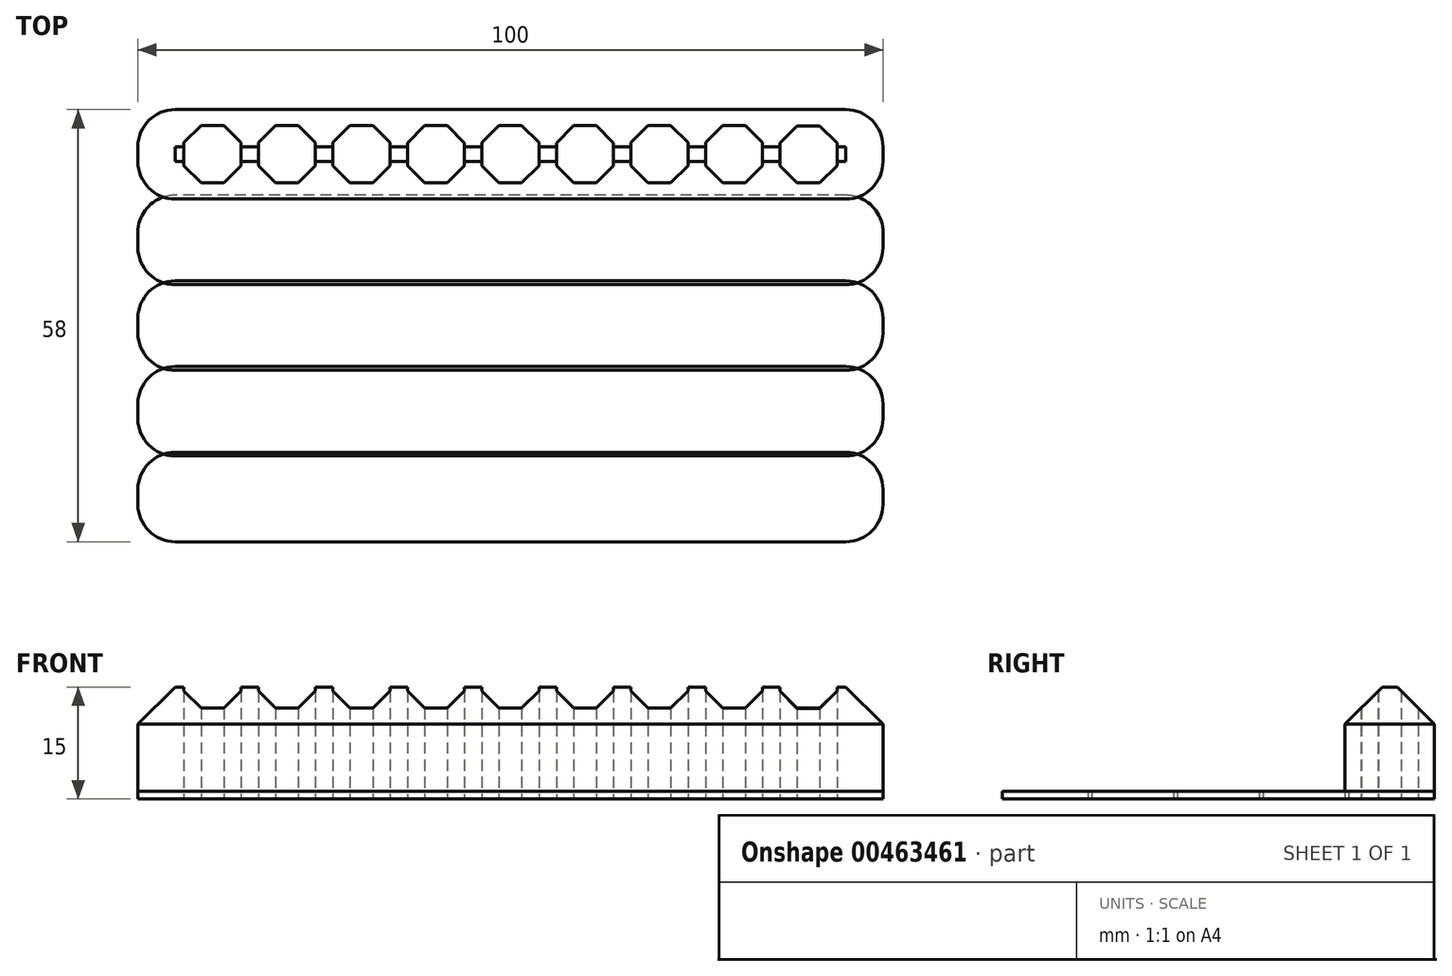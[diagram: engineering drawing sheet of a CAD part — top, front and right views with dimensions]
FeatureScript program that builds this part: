
annotation { "Feature Type Name" : "Feature", "Feature Type Description" : "" }
export const myFeature = defineFeature(function(context is Context, id is Id, definition is map)
    precondition{}
    {
        {
            var Q0;
            Q0=qCreatedBy(makeId("Top.planeOp"),FACE);
            var sketch = newSketch(context, id + "F0", { "sketchPlane" : qUnion([Q0])});
            skLineSegment(sketch, "E0.bottom", {"start": v(50, -6) * mm, "end": v(-50, -6) * mm});
            skLineSegment(sketch, "E0.top", {"start": v(50, 6) * mm, "end": v(-50, 6) * mm});
            skLineSegment(sketch, "E0.left", {"start": v(50, -6) * mm, "end": v(50, 6) * mm});
            skLineSegment(sketch, "E0.right", {"start": v(-50, -6) * mm, "end": v(-50, 6) * mm});
            skPoint(sketch, "E0.middle", {"position": v(0, 0) * mm});
            skPoint(sketch, "E1.middle", {"position": v(-40, 0) * mm});
            skLineSegment(sketch, "E2.bottom", {"start": v(-41.53, 3.83) * mm, "end": v(-38.47, 3.83) * mm});
            skLineSegment(sketch, "E2.top", {"start": v(-41.53, -3.83) * mm, "end": v(-38.47, -3.83) * mm});
            skLineSegment(sketch, "E2.left", {"start": v(-41.53, 3.83) * mm, "end": v(-41.53, -3.83) * mm});
            skLineSegment(sketch, "E2.right", {"start": v(-38.47, 3.83) * mm, "end": v(-38.47, -3.83) * mm});
            skLineSegment(sketch, "E3.bottom", {"start": v(-36.17, -1.54) * mm, "end": v(-43.83, -1.54) * mm});
            skLineSegment(sketch, "E3.top", {"start": v(-36.17, 1.54) * mm, "end": v(-43.83, 1.54) * mm});
            skLineSegment(sketch, "E3.left", {"start": v(-36.17, -1.54) * mm, "end": v(-36.17, 1.54) * mm});
            skLineSegment(sketch, "E3.right", {"start": v(-43.83, -1.54) * mm, "end": v(-43.83, 1.54) * mm});
            skPoint(sketch, "E4.middle", {"position": v(-30, 0) * mm});
            skLineSegment(sketch, "E5.bottom", {"start": v(-31.53, 3.83) * mm, "end": v(-28.47, 3.83) * mm});
            skLineSegment(sketch, "E5.top", {"start": v(-31.53, -3.83) * mm, "end": v(-28.47, -3.83) * mm});
            skLineSegment(sketch, "E5.left", {"start": v(-31.53, 3.83) * mm, "end": v(-31.53, -3.83) * mm});
            skLineSegment(sketch, "E5.right", {"start": v(-28.47, 3.83) * mm, "end": v(-28.47, -3.83) * mm});
            skLineSegment(sketch, "E6.bottom", {"start": v(-26.17, -1.54) * mm, "end": v(-33.83, -1.54) * mm});
            skLineSegment(sketch, "E6.top", {"start": v(-26.17, 1.54) * mm, "end": v(-33.83, 1.54) * mm});
            skLineSegment(sketch, "E6.left", {"start": v(-26.17, -1.54) * mm, "end": v(-26.17, 1.54) * mm});
            skLineSegment(sketch, "E6.right", {"start": v(-33.83, -1.54) * mm, "end": v(-33.83, 1.54) * mm});
            skPoint(sketch, "E7.middle", {"position": v(-20, 0) * mm});
            skLineSegment(sketch, "E8.bottom", {"start": v(-21.53, 3.84) * mm, "end": v(-18.48, 3.84) * mm});
            skLineSegment(sketch, "E8.top", {"start": v(-21.53, -3.83) * mm, "end": v(-18.48, -3.83) * mm});
            skLineSegment(sketch, "E8.left", {"start": v(-21.53, 3.84) * mm, "end": v(-21.53, -3.83) * mm});
            skLineSegment(sketch, "E8.right", {"start": v(-18.48, 3.84) * mm, "end": v(-18.48, -3.83) * mm});
            skLineSegment(sketch, "E9.bottom", {"start": v(-16.18, -1.53) * mm, "end": v(-23.83, -1.53) * mm});
            skLineSegment(sketch, "E9.top", {"start": v(-16.18, 1.54) * mm, "end": v(-23.83, 1.54) * mm});
            skLineSegment(sketch, "E9.left", {"start": v(-16.18, -1.53) * mm, "end": v(-16.18, 1.54) * mm});
            skLineSegment(sketch, "E9.right", {"start": v(-23.83, -1.53) * mm, "end": v(-23.83, 1.54) * mm});
            skPoint(sketch, "E10.middle", {"position": v(-9.99, 0) * mm});
            skLineSegment(sketch, "E11.bottom", {"start": v(-11.52, 3.83) * mm, "end": v(-8.46, 3.83) * mm});
            skLineSegment(sketch, "E11.top", {"start": v(-11.52, -3.84) * mm, "end": v(-8.46, -3.84) * mm});
            skLineSegment(sketch, "E11.left", {"start": v(-11.52, 3.83) * mm, "end": v(-11.52, -3.84) * mm});
            skLineSegment(sketch, "E11.right", {"start": v(-8.46, 3.83) * mm, "end": v(-8.46, -3.84) * mm});
            skLineSegment(sketch, "E12.bottom", {"start": v(-6.16, -1.54) * mm, "end": v(-13.82, -1.54) * mm});
            skLineSegment(sketch, "E12.top", {"start": v(-6.16, 1.53) * mm, "end": v(-13.82, 1.53) * mm});
            skLineSegment(sketch, "E12.left", {"start": v(-6.16, -1.54) * mm, "end": v(-6.16, 1.53) * mm});
            skLineSegment(sketch, "E12.right", {"start": v(-13.82, -1.54) * mm, "end": v(-13.82, 1.53) * mm});
            skPoint(sketch, "E13.middle", {"position": v(0, 0.02) * mm});
            skLineSegment(sketch, "E14.bottom", {"start": v(-1.53, 3.86) * mm, "end": v(1.52, 3.86) * mm});
            skLineSegment(sketch, "E14.top", {"start": v(-1.53, -3.8) * mm, "end": v(1.52, -3.8) * mm});
            skLineSegment(sketch, "E14.left", {"start": v(-1.53, 3.86) * mm, "end": v(-1.53, -3.8) * mm});
            skLineSegment(sketch, "E14.right", {"start": v(1.52, 3.86) * mm, "end": v(1.52, -3.8) * mm});
            skLineSegment(sketch, "E15.bottom", {"start": v(3.82, -1.51) * mm, "end": v(-3.83, -1.51) * mm});
            skLineSegment(sketch, "E15.top", {"start": v(3.82, 1.56) * mm, "end": v(-3.83, 1.56) * mm});
            skLineSegment(sketch, "E15.left", {"start": v(3.82, -1.51) * mm, "end": v(3.82, 1.56) * mm});
            skLineSegment(sketch, "E15.right", {"start": v(-3.83, -1.51) * mm, "end": v(-3.83, 1.56) * mm});
            skPoint(sketch, "E16.middle", {"position": v(10, 0) * mm});
            skLineSegment(sketch, "E17.bottom", {"start": v(8.48, 3.83) * mm, "end": v(11.53, 3.83) * mm});
            skLineSegment(sketch, "E17.top", {"start": v(8.48, -3.84) * mm, "end": v(11.53, -3.84) * mm});
            skLineSegment(sketch, "E17.left", {"start": v(8.48, 3.83) * mm, "end": v(8.48, -3.84) * mm});
            skLineSegment(sketch, "E17.right", {"start": v(11.53, 3.83) * mm, "end": v(11.53, -3.84) * mm});
            skLineSegment(sketch, "E18.bottom", {"start": v(13.83, -1.54) * mm, "end": v(6.18, -1.54) * mm});
            skLineSegment(sketch, "E18.top", {"start": v(13.83, 1.53) * mm, "end": v(6.18, 1.53) * mm});
            skLineSegment(sketch, "E18.left", {"start": v(13.83, -1.54) * mm, "end": v(13.83, 1.53) * mm});
            skLineSegment(sketch, "E18.right", {"start": v(6.18, -1.54) * mm, "end": v(6.18, 1.53) * mm});
            skPoint(sketch, "E19.middle", {"position": v(19.99, 0) * mm});
            skLineSegment(sketch, "E20.bottom", {"start": v(18.46, 3.84) * mm, "end": v(21.51, 3.84) * mm});
            skLineSegment(sketch, "E20.top", {"start": v(18.46, -3.82) * mm, "end": v(21.51, -3.82) * mm});
            skLineSegment(sketch, "E20.left", {"start": v(18.46, 3.84) * mm, "end": v(18.46, -3.82) * mm});
            skLineSegment(sketch, "E20.right", {"start": v(21.51, 3.84) * mm, "end": v(21.51, -3.82) * mm});
            skLineSegment(sketch, "E21.bottom", {"start": v(23.82, -1.53) * mm, "end": v(16.16, -1.53) * mm});
            skLineSegment(sketch, "E21.top", {"start": v(23.82, 1.55) * mm, "end": v(16.16, 1.55) * mm});
            skLineSegment(sketch, "E21.left", {"start": v(23.82, -1.53) * mm, "end": v(23.82, 1.55) * mm});
            skLineSegment(sketch, "E21.right", {"start": v(16.16, -1.53) * mm, "end": v(16.16, 1.55) * mm});
            skPoint(sketch, "E22.middle", {"position": v(30, 0) * mm});
            skLineSegment(sketch, "E23.bottom", {"start": v(28.47, 3.84) * mm, "end": v(31.53, 3.84) * mm});
            skLineSegment(sketch, "E23.top", {"start": v(28.47, -3.82) * mm, "end": v(31.53, -3.82) * mm});
            skLineSegment(sketch, "E23.left", {"start": v(28.47, 3.84) * mm, "end": v(28.47, -3.82) * mm});
            skLineSegment(sketch, "E23.right", {"start": v(31.53, 3.84) * mm, "end": v(31.53, -3.82) * mm});
            skLineSegment(sketch, "E24.bottom", {"start": v(33.83, -1.53) * mm, "end": v(26.17, -1.53) * mm});
            skLineSegment(sketch, "E24.top", {"start": v(33.83, 1.55) * mm, "end": v(26.17, 1.55) * mm});
            skLineSegment(sketch, "E24.left", {"start": v(33.83, -1.53) * mm, "end": v(33.83, 1.55) * mm});
            skLineSegment(sketch, "E24.right", {"start": v(26.17, -1.53) * mm, "end": v(26.17, 1.55) * mm});
            skPoint(sketch, "E25.middle", {"position": v(40, -0.02) * mm});
            skLineSegment(sketch, "E26.bottom", {"start": v(38.47, 3.81) * mm, "end": v(41.52, 3.81) * mm});
            skLineSegment(sketch, "E26.top", {"start": v(38.47, -3.85) * mm, "end": v(41.52, -3.85) * mm});
            skLineSegment(sketch, "E26.left", {"start": v(38.47, 3.81) * mm, "end": v(38.47, -3.85) * mm});
            skLineSegment(sketch, "E26.right", {"start": v(41.52, 3.81) * mm, "end": v(41.52, -3.85) * mm});
            skLineSegment(sketch, "E27.bottom", {"start": v(43.82, -1.56) * mm, "end": v(36.17, -1.56) * mm});
            skLineSegment(sketch, "E27.top", {"start": v(43.82, 1.52) * mm, "end": v(36.17, 1.52) * mm});
            skLineSegment(sketch, "E27.left", {"start": v(43.82, -1.56) * mm, "end": v(43.82, 1.52) * mm});
            skLineSegment(sketch, "E27.right", {"start": v(36.17, -1.56) * mm, "end": v(36.17, 1.52) * mm});
            skLineSegment(sketch, "E28", {"start": v(-41.53, 3.83) * mm, "end": v(-43.83, 1.54) * mm});
            skLineSegment(sketch, "E29", {"start": v(-43.83, -1.54) * mm, "end": v(-41.53, -3.83) * mm});
            skLineSegment(sketch, "E30", {"start": v(-38.47, -3.83) * mm, "end": v(-36.17, -1.54) * mm});
            skLineSegment(sketch, "E31", {"start": v(-36.17, 1.54) * mm, "end": v(-38.47, 3.83) * mm});
            skLineSegment(sketch, "E32", {"start": v(-33.83, 1.54) * mm, "end": v(-31.53, 3.83) * mm});
            skLineSegment(sketch, "E33", {"start": v(-28.47, 3.83) * mm, "end": v(-26.17, 1.54) * mm});
            skLineSegment(sketch, "E34", {"start": v(-26.17, -1.54) * mm, "end": v(-28.47, -3.83) * mm});
            skLineSegment(sketch, "E35", {"start": v(-31.53, -3.83) * mm, "end": v(-33.83, -1.54) * mm});
            skLineSegment(sketch, "E36", {"start": v(-23.83, 1.54) * mm, "end": v(-21.53, 3.84) * mm});
            skLineSegment(sketch, "E37", {"start": v(-18.48, 3.84) * mm, "end": v(-16.18, 1.54) * mm});
            skLineSegment(sketch, "E38", {"start": v(-16.18, -1.53) * mm, "end": v(-18.48, -3.83) * mm});
            skLineSegment(sketch, "E39", {"start": v(-21.53, -3.83) * mm, "end": v(-23.83, -1.53) * mm});
            skLineSegment(sketch, "E40", {"start": v(-13.82, -1.54) * mm, "end": v(-11.52, -3.84) * mm});
            skLineSegment(sketch, "E41", {"start": v(-13.82, 1.53) * mm, "end": v(-11.52, 3.83) * mm});
            skLineSegment(sketch, "E42", {"start": v(-8.46, 3.83) * mm, "end": v(-6.16, 1.53) * mm});
            skLineSegment(sketch, "E43", {"start": v(-6.16, -1.54) * mm, "end": v(-8.46, -3.84) * mm});
            skLineSegment(sketch, "E44", {"start": v(-3.83, -1.51) * mm, "end": v(-1.53, -3.8) * mm});
            skLineSegment(sketch, "E45", {"start": v(-3.83, 1.56) * mm, "end": v(-1.53, 3.86) * mm});
            skLineSegment(sketch, "E46", {"start": v(1.52, 3.86) * mm, "end": v(3.82, 1.56) * mm});
            skLineSegment(sketch, "E47", {"start": v(3.82, -1.51) * mm, "end": v(1.52, -3.8) * mm});
            skLineSegment(sketch, "E48", {"start": v(6.18, 1.53) * mm, "end": v(8.48, 3.83) * mm});
            skLineSegment(sketch, "E49", {"start": v(11.53, 3.83) * mm, "end": v(13.83, 1.53) * mm});
            skLineSegment(sketch, "E50", {"start": v(13.83, -1.54) * mm, "end": v(11.53, -3.84) * mm});
            skLineSegment(sketch, "E51", {"start": v(8.48, -3.84) * mm, "end": v(6.18, -1.54) * mm});
            skLineSegment(sketch, "E52", {"start": v(16.16, 1.55) * mm, "end": v(18.46, 3.84) * mm});
            skLineSegment(sketch, "E53", {"start": v(21.51, 3.84) * mm, "end": v(23.82, 1.55) * mm});
            skLineSegment(sketch, "E54", {"start": v(23.82, -1.53) * mm, "end": v(21.51, -3.82) * mm});
            skLineSegment(sketch, "E55", {"start": v(18.46, -3.82) * mm, "end": v(16.16, -1.53) * mm});
            skLineSegment(sketch, "E56", {"start": v(26.17, 1.55) * mm, "end": v(28.47, 3.84) * mm});
            skLineSegment(sketch, "E57", {"start": v(31.53, 3.84) * mm, "end": v(33.83, 1.55) * mm});
            skLineSegment(sketch, "E58", {"start": v(33.83, -1.53) * mm, "end": v(31.53, -3.82) * mm});
            skLineSegment(sketch, "E59", {"start": v(28.47, -3.82) * mm, "end": v(26.17, -1.53) * mm});
            skLineSegment(sketch, "E60", {"start": v(36.17, 1.52) * mm, "end": v(38.47, 3.81) * mm});
            skLineSegment(sketch, "E61", {"start": v(41.52, 3.81) * mm, "end": v(43.82, 1.52) * mm});
            skLineSegment(sketch, "E62", {"start": v(43.82, -1.56) * mm, "end": v(41.52, -3.85) * mm});
            skLineSegment(sketch, "E63", {"start": v(38.47, -3.85) * mm, "end": v(36.17, -1.56) * mm});
            skSolve(sketch);
        }
        {
            var Q0;
            Q0=makeQuery(id+"F0.imprint","IMPRINT",FACE,{"disambiguationData":[TD([[makeQuery(id+"F0.imprint","IMPRINT",EDGE,{"derivedFrom":sQuery(id+"F0.wireOp",EDGE,"E0.bottom")}),-1.0]])]});
            extrude(context, id + "F1", {"entities" : qUnion([Q0]), "depth" : 15 * mm});
        }
        {
            var Q0;
            Q0=makeQuery(id+"F0.imprint","IMPRINT",FACE,{"disambiguationData":[TD([[makeQuery(id+"F0.imprint","IMPRINT",EDGE,{"derivedFrom":sQuery(id+"F0.wireOp",EDGE,"E0.bottom")}),-1.0]])]});
            var Q1;
            {var subQ5=sQuery(id+"F0.wireOp",EDGE,"E3.right");Q1=makeQuery(id+"F0.imprint","IMPRINT",FACE,{"disambiguationData":[TD([[makeQuery(id+"F0.imprint","IMPRINT",EDGE,{"derivedFrom":subQ5}),-1.0]])]});}
            var Q2;
            {var subQ0=sQuery(id+"F0.wireOp",EDGE,"E28");Q2=makeQuery(id+"F0.imprint","IMPRINT",FACE,{"disambiguationData":[TD([[makeQuery(id+"F0.imprint","IMPRINT",EDGE,{"derivedFrom":subQ0}),1.0]])]});}
            var Q3;
            {var subQ0=sQuery(id+"F0.wireOp",EDGE,"E2.bottom");Q3=makeQuery(id+"F0.imprint","IMPRINT",FACE,{"disambiguationData":[TD([[makeQuery(id+"F0.imprint","IMPRINT",EDGE,{"derivedFrom":subQ0}),-1.0]])]});}
            var Q4;
            {var subQ0=sQuery(id+"F0.wireOp",EDGE,"E29");Q4=makeQuery(id+"F0.imprint","IMPRINT",FACE,{"disambiguationData":[TD([[makeQuery(id+"F0.imprint","IMPRINT",EDGE,{"derivedFrom":subQ0}),1.0]])]});}
            var Q5;
            {var subQ0=sQuery(id+"F0.wireOp",EDGE,"E2.top");Q5=makeQuery(id+"F0.imprint","IMPRINT",FACE,{"disambiguationData":[TD([[makeQuery(id+"F0.imprint","IMPRINT",EDGE,{"derivedFrom":subQ0}),1.0]])]});}
            var Q6;
            {var subQ0=sQuery(id+"F0.wireOp",EDGE,"E3.top");var subQ1=sQuery(id+"F0.wireOp",EDGE,"E2.left");var subQ2=makeQuery(id+"F0.imprint","INTERSECT",VERTEX,{"derivedFrom":[subQ1,subQ0]});Q6=makeQuery(id+"F0.imprint","IMPRINT",FACE,{"disambiguationData":[TD([[makeQuery(id+"F0.imprint","IMPRINT",EDGE,{"disambiguationData":[TD([[subQ2,-1.0]])],"derivedFrom":subQ1}),1.0]])]});}
            var Q7;
            {var subQ5=sQuery(id+"F0.wireOp",EDGE,"E3.left");Q7=makeQuery(id+"F0.imprint","IMPRINT",FACE,{"disambiguationData":[TD([[makeQuery(id+"F0.imprint","IMPRINT",EDGE,{"derivedFrom":subQ5}),1.0]])]});}
            var Q8;
            {var subQ0=sQuery(id+"F0.wireOp",EDGE,"E31");Q8=makeQuery(id+"F0.imprint","IMPRINT",FACE,{"disambiguationData":[TD([[makeQuery(id+"F0.imprint","IMPRINT",EDGE,{"derivedFrom":subQ0}),1.0]])]});}
            var Q9;
            {var subQ0=sQuery(id+"F0.wireOp",EDGE,"E30");Q9=makeQuery(id+"F0.imprint","IMPRINT",FACE,{"disambiguationData":[TD([[makeQuery(id+"F0.imprint","IMPRINT",EDGE,{"derivedFrom":subQ0}),1.0]])]});}
            var Q10;
            {var subQ0=sQuery(id+"F0.wireOp",EDGE,"E35");Q10=makeQuery(id+"F0.imprint","IMPRINT",FACE,{"disambiguationData":[TD([[makeQuery(id+"F0.imprint","IMPRINT",EDGE,{"derivedFrom":subQ0}),-1.0]])]});}
            var Q11;
            {var subQ5=sQuery(id+"F0.wireOp",EDGE,"E6.right");Q11=makeQuery(id+"F0.imprint","IMPRINT",FACE,{"disambiguationData":[TD([[makeQuery(id+"F0.imprint","IMPRINT",EDGE,{"derivedFrom":subQ5}),-1.0]])]});}
            var Q12;
            {var subQ0=sQuery(id+"F0.wireOp",EDGE,"E32");Q12=makeQuery(id+"F0.imprint","IMPRINT",FACE,{"disambiguationData":[TD([[makeQuery(id+"F0.imprint","IMPRINT",EDGE,{"derivedFrom":subQ0}),-1.0]])]});}
            var Q13;
            {var subQ0=sQuery(id+"F0.wireOp",EDGE,"E5.bottom");Q13=makeQuery(id+"F0.imprint","IMPRINT",FACE,{"disambiguationData":[TD([[makeQuery(id+"F0.imprint","IMPRINT",EDGE,{"derivedFrom":subQ0}),-1.0]])]});}
            var Q14;
            {var subQ0=sQuery(id+"F0.wireOp",EDGE,"E33");Q14=makeQuery(id+"F0.imprint","IMPRINT",FACE,{"disambiguationData":[TD([[makeQuery(id+"F0.imprint","IMPRINT",EDGE,{"derivedFrom":subQ0}),-1.0]])]});}
            var Q15;
            {var subQ5=sQuery(id+"F0.wireOp",EDGE,"E6.left");Q15=makeQuery(id+"F0.imprint","IMPRINT",FACE,{"disambiguationData":[TD([[makeQuery(id+"F0.imprint","IMPRINT",EDGE,{"derivedFrom":subQ5}),1.0]])]});}
            var Q16;
            {var subQ0=sQuery(id+"F0.wireOp",EDGE,"E6.top");var subQ1=sQuery(id+"F0.wireOp",EDGE,"E5.left");var subQ2=makeQuery(id+"F0.imprint","INTERSECT",VERTEX,{"derivedFrom":[subQ1,subQ0]});Q16=makeQuery(id+"F0.imprint","IMPRINT",FACE,{"disambiguationData":[TD([[makeQuery(id+"F0.imprint","IMPRINT",EDGE,{"disambiguationData":[TD([[subQ2,-1.0]])],"derivedFrom":subQ1}),1.0]])]});}
            var Q17;
            {var subQ0=sQuery(id+"F0.wireOp",EDGE,"E5.top");Q17=makeQuery(id+"F0.imprint","IMPRINT",FACE,{"disambiguationData":[TD([[makeQuery(id+"F0.imprint","IMPRINT",EDGE,{"derivedFrom":subQ0}),1.0]])]});}
            var Q18;
            {var subQ0=sQuery(id+"F0.wireOp",EDGE,"E34");Q18=makeQuery(id+"F0.imprint","IMPRINT",FACE,{"disambiguationData":[TD([[makeQuery(id+"F0.imprint","IMPRINT",EDGE,{"derivedFrom":subQ0}),-1.0]])]});}
            var Q19;
            {var subQ0=sQuery(id+"F0.wireOp",EDGE,"E39");Q19=makeQuery(id+"F0.imprint","IMPRINT",FACE,{"disambiguationData":[TD([[makeQuery(id+"F0.imprint","IMPRINT",EDGE,{"derivedFrom":subQ0}),-1.0]])]});}
            var Q20;
            {var subQ5=sQuery(id+"F0.wireOp",EDGE,"E9.right");Q20=makeQuery(id+"F0.imprint","IMPRINT",FACE,{"disambiguationData":[TD([[makeQuery(id+"F0.imprint","IMPRINT",EDGE,{"derivedFrom":subQ5}),-1.0]])]});}
            var Q21;
            {var subQ0=sQuery(id+"F0.wireOp",EDGE,"E36");Q21=makeQuery(id+"F0.imprint","IMPRINT",FACE,{"disambiguationData":[TD([[makeQuery(id+"F0.imprint","IMPRINT",EDGE,{"derivedFrom":subQ0}),-1.0]])]});}
            var Q22;
            {var subQ0=sQuery(id+"F0.wireOp",EDGE,"E8.bottom");Q22=makeQuery(id+"F0.imprint","IMPRINT",FACE,{"disambiguationData":[TD([[makeQuery(id+"F0.imprint","IMPRINT",EDGE,{"derivedFrom":subQ0}),-1.0]])]});}
            var Q23;
            {var subQ0=sQuery(id+"F0.wireOp",EDGE,"E9.top");var subQ1=sQuery(id+"F0.wireOp",EDGE,"E8.left");var subQ2=makeQuery(id+"F0.imprint","INTERSECT",VERTEX,{"derivedFrom":[subQ1,subQ0]});Q23=makeQuery(id+"F0.imprint","IMPRINT",FACE,{"disambiguationData":[TD([[makeQuery(id+"F0.imprint","IMPRINT",EDGE,{"disambiguationData":[TD([[subQ2,-1.0]])],"derivedFrom":subQ1}),1.0]])]});}
            var Q24;
            {var subQ0=sQuery(id+"F0.wireOp",EDGE,"E8.top");Q24=makeQuery(id+"F0.imprint","IMPRINT",FACE,{"disambiguationData":[TD([[makeQuery(id+"F0.imprint","IMPRINT",EDGE,{"derivedFrom":subQ0}),1.0]])]});}
            var Q25;
            {var subQ0=sQuery(id+"F0.wireOp",EDGE,"E38");Q25=makeQuery(id+"F0.imprint","IMPRINT",FACE,{"disambiguationData":[TD([[makeQuery(id+"F0.imprint","IMPRINT",EDGE,{"derivedFrom":subQ0}),-1.0]])]});}
            var Q26;
            {var subQ5=sQuery(id+"F0.wireOp",EDGE,"E9.left");Q26=makeQuery(id+"F0.imprint","IMPRINT",FACE,{"disambiguationData":[TD([[makeQuery(id+"F0.imprint","IMPRINT",EDGE,{"derivedFrom":subQ5}),1.0]])]});}
            var Q27;
            {var subQ0=sQuery(id+"F0.wireOp",EDGE,"E37");Q27=makeQuery(id+"F0.imprint","IMPRINT",FACE,{"disambiguationData":[TD([[makeQuery(id+"F0.imprint","IMPRINT",EDGE,{"derivedFrom":subQ0}),-1.0]])]});}
            var Q28;
            {var subQ0=sQuery(id+"F0.wireOp",EDGE,"E41");Q28=makeQuery(id+"F0.imprint","IMPRINT",FACE,{"disambiguationData":[TD([[makeQuery(id+"F0.imprint","IMPRINT",EDGE,{"derivedFrom":subQ0}),-1.0]])]});}
            var Q29;
            {var subQ5=sQuery(id+"F0.wireOp",EDGE,"E12.right");Q29=makeQuery(id+"F0.imprint","IMPRINT",FACE,{"disambiguationData":[TD([[makeQuery(id+"F0.imprint","IMPRINT",EDGE,{"derivedFrom":subQ5}),-1.0]])]});}
            var Q30;
            {var subQ0=sQuery(id+"F0.wireOp",EDGE,"E40");Q30=makeQuery(id+"F0.imprint","IMPRINT",FACE,{"disambiguationData":[TD([[makeQuery(id+"F0.imprint","IMPRINT",EDGE,{"derivedFrom":subQ0}),1.0]])]});}
            var Q31;
            {var subQ0=sQuery(id+"F0.wireOp",EDGE,"E11.top");Q31=makeQuery(id+"F0.imprint","IMPRINT",FACE,{"disambiguationData":[TD([[makeQuery(id+"F0.imprint","IMPRINT",EDGE,{"derivedFrom":subQ0}),1.0]])]});}
            var Q32;
            {var subQ0=sQuery(id+"F0.wireOp",EDGE,"E11.bottom");Q32=makeQuery(id+"F0.imprint","IMPRINT",FACE,{"disambiguationData":[TD([[makeQuery(id+"F0.imprint","IMPRINT",EDGE,{"derivedFrom":subQ0}),-1.0]])]});}
            var Q33;
            {var subQ5=sQuery(id+"F0.wireOp",EDGE,"E12.left");Q33=makeQuery(id+"F0.imprint","IMPRINT",FACE,{"disambiguationData":[TD([[makeQuery(id+"F0.imprint","IMPRINT",EDGE,{"derivedFrom":subQ5}),1.0]])]});}
            var Q34;
            {var subQ0=sQuery(id+"F0.wireOp",EDGE,"E42");Q34=makeQuery(id+"F0.imprint","IMPRINT",FACE,{"disambiguationData":[TD([[makeQuery(id+"F0.imprint","IMPRINT",EDGE,{"derivedFrom":subQ0}),-1.0]])]});}
            var Q35;
            {var subQ0=sQuery(id+"F0.wireOp",EDGE,"E43");Q35=makeQuery(id+"F0.imprint","IMPRINT",FACE,{"disambiguationData":[TD([[makeQuery(id+"F0.imprint","IMPRINT",EDGE,{"derivedFrom":subQ0}),-1.0]])]});}
            var Q36;
            {var subQ0=sQuery(id+"F0.wireOp",EDGE,"E12.top");var subQ1=sQuery(id+"F0.wireOp",EDGE,"E11.left");var subQ2=makeQuery(id+"F0.imprint","INTERSECT",VERTEX,{"derivedFrom":[subQ1,subQ0]});Q36=makeQuery(id+"F0.imprint","IMPRINT",FACE,{"disambiguationData":[TD([[makeQuery(id+"F0.imprint","IMPRINT",EDGE,{"disambiguationData":[TD([[subQ2,-1.0]])],"derivedFrom":subQ1}),1.0]])]});}
            var Q37;
            {var subQ0=sQuery(id+"F0.wireOp",EDGE,"E45");Q37=makeQuery(id+"F0.imprint","IMPRINT",FACE,{"disambiguationData":[TD([[makeQuery(id+"F0.imprint","IMPRINT",EDGE,{"derivedFrom":subQ0}),-1.0]])]});}
            var Q38;
            {var subQ0=sQuery(id+"F0.wireOp",EDGE,"E14.bottom");Q38=makeQuery(id+"F0.imprint","IMPRINT",FACE,{"disambiguationData":[TD([[makeQuery(id+"F0.imprint","IMPRINT",EDGE,{"derivedFrom":subQ0}),-1.0]])]});}
            var Q39;
            {var subQ0=sQuery(id+"F0.wireOp",EDGE,"E46");Q39=makeQuery(id+"F0.imprint","IMPRINT",FACE,{"disambiguationData":[TD([[makeQuery(id+"F0.imprint","IMPRINT",EDGE,{"derivedFrom":subQ0}),-1.0]])]});}
            var Q40;
            {var subQ5=sQuery(id+"F0.wireOp",EDGE,"E15.left");Q40=makeQuery(id+"F0.imprint","IMPRINT",FACE,{"disambiguationData":[TD([[makeQuery(id+"F0.imprint","IMPRINT",EDGE,{"derivedFrom":subQ5}),1.0]])]});}
            var Q41;
            {var subQ0=sQuery(id+"F0.wireOp",EDGE,"E15.top");var subQ1=sQuery(id+"F0.wireOp",EDGE,"E14.left");var subQ2=makeQuery(id+"F0.imprint","INTERSECT",VERTEX,{"derivedFrom":[subQ1,subQ0]});Q41=makeQuery(id+"F0.imprint","IMPRINT",FACE,{"disambiguationData":[TD([[makeQuery(id+"F0.imprint","IMPRINT",EDGE,{"disambiguationData":[TD([[subQ2,-1.0]])],"derivedFrom":subQ1}),1.0]])]});}
            var Q42;
            {var subQ5=sQuery(id+"F0.wireOp",EDGE,"E15.right");Q42=makeQuery(id+"F0.imprint","IMPRINT",FACE,{"disambiguationData":[TD([[makeQuery(id+"F0.imprint","IMPRINT",EDGE,{"derivedFrom":subQ5}),-1.0]])]});}
            var Q43;
            {var subQ0=sQuery(id+"F0.wireOp",EDGE,"E14.top");Q43=makeQuery(id+"F0.imprint","IMPRINT",FACE,{"disambiguationData":[TD([[makeQuery(id+"F0.imprint","IMPRINT",EDGE,{"derivedFrom":subQ0}),1.0]])]});}
            var Q44;
            {var subQ0=sQuery(id+"F0.wireOp",EDGE,"E47");Q44=makeQuery(id+"F0.imprint","IMPRINT",FACE,{"disambiguationData":[TD([[makeQuery(id+"F0.imprint","IMPRINT",EDGE,{"derivedFrom":subQ0}),-1.0]])]});}
            var Q45;
            {var subQ0=sQuery(id+"F0.wireOp",EDGE,"E44");Q45=makeQuery(id+"F0.imprint","IMPRINT",FACE,{"disambiguationData":[TD([[makeQuery(id+"F0.imprint","IMPRINT",EDGE,{"derivedFrom":subQ0}),1.0]])]});}
            var Q46;
            {var subQ5=sQuery(id+"F0.wireOp",EDGE,"E18.right");Q46=makeQuery(id+"F0.imprint","IMPRINT",FACE,{"disambiguationData":[TD([[makeQuery(id+"F0.imprint","IMPRINT",EDGE,{"derivedFrom":subQ5}),-1.0]])]});}
            var Q47;
            {var subQ0=sQuery(id+"F0.wireOp",EDGE,"E48");Q47=makeQuery(id+"F0.imprint","IMPRINT",FACE,{"disambiguationData":[TD([[makeQuery(id+"F0.imprint","IMPRINT",EDGE,{"derivedFrom":subQ0}),-1.0]])]});}
            var Q48;
            {var subQ0=sQuery(id+"F0.wireOp",EDGE,"E17.bottom");Q48=makeQuery(id+"F0.imprint","IMPRINT",FACE,{"disambiguationData":[TD([[makeQuery(id+"F0.imprint","IMPRINT",EDGE,{"derivedFrom":subQ0}),-1.0]])]});}
            var Q49;
            {var subQ0=sQuery(id+"F0.wireOp",EDGE,"E49");Q49=makeQuery(id+"F0.imprint","IMPRINT",FACE,{"disambiguationData":[TD([[makeQuery(id+"F0.imprint","IMPRINT",EDGE,{"derivedFrom":subQ0}),-1.0]])]});}
            var Q50;
            {var subQ5=sQuery(id+"F0.wireOp",EDGE,"E18.left");Q50=makeQuery(id+"F0.imprint","IMPRINT",FACE,{"disambiguationData":[TD([[makeQuery(id+"F0.imprint","IMPRINT",EDGE,{"derivedFrom":subQ5}),1.0]])]});}
            var Q51;
            {var subQ0=sQuery(id+"F0.wireOp",EDGE,"E18.top");var subQ1=sQuery(id+"F0.wireOp",EDGE,"E17.left");var subQ2=makeQuery(id+"F0.imprint","INTERSECT",VERTEX,{"derivedFrom":[subQ1,subQ0]});Q51=makeQuery(id+"F0.imprint","IMPRINT",FACE,{"disambiguationData":[TD([[makeQuery(id+"F0.imprint","IMPRINT",EDGE,{"disambiguationData":[TD([[subQ2,-1.0]])],"derivedFrom":subQ1}),1.0]])]});}
            var Q52;
            {var subQ0=sQuery(id+"F0.wireOp",EDGE,"E51");Q52=makeQuery(id+"F0.imprint","IMPRINT",FACE,{"disambiguationData":[TD([[makeQuery(id+"F0.imprint","IMPRINT",EDGE,{"derivedFrom":subQ0}),-1.0]])]});}
            var Q53;
            {var subQ0=sQuery(id+"F0.wireOp",EDGE,"E17.top");Q53=makeQuery(id+"F0.imprint","IMPRINT",FACE,{"disambiguationData":[TD([[makeQuery(id+"F0.imprint","IMPRINT",EDGE,{"derivedFrom":subQ0}),1.0]])]});}
            var Q54;
            {var subQ0=sQuery(id+"F0.wireOp",EDGE,"E50");Q54=makeQuery(id+"F0.imprint","IMPRINT",FACE,{"disambiguationData":[TD([[makeQuery(id+"F0.imprint","IMPRINT",EDGE,{"derivedFrom":subQ0}),-1.0]])]});}
            var Q55;
            {var subQ5=sQuery(id+"F0.wireOp",EDGE,"E21.right");Q55=makeQuery(id+"F0.imprint","IMPRINT",FACE,{"disambiguationData":[TD([[makeQuery(id+"F0.imprint","IMPRINT",EDGE,{"derivedFrom":subQ5}),-1.0]])]});}
            var Q56;
            {var subQ0=sQuery(id+"F0.wireOp",EDGE,"E55");Q56=makeQuery(id+"F0.imprint","IMPRINT",FACE,{"disambiguationData":[TD([[makeQuery(id+"F0.imprint","IMPRINT",EDGE,{"derivedFrom":subQ0}),-1.0]])]});}
            var Q57;
            {var subQ0=sQuery(id+"F0.wireOp",EDGE,"E20.top");Q57=makeQuery(id+"F0.imprint","IMPRINT",FACE,{"disambiguationData":[TD([[makeQuery(id+"F0.imprint","IMPRINT",EDGE,{"derivedFrom":subQ0}),1.0]])]});}
            var Q58;
            {var subQ0=sQuery(id+"F0.wireOp",EDGE,"E54");Q58=makeQuery(id+"F0.imprint","IMPRINT",FACE,{"disambiguationData":[TD([[makeQuery(id+"F0.imprint","IMPRINT",EDGE,{"derivedFrom":subQ0}),-1.0]])]});}
            var Q59;
            {var subQ5=sQuery(id+"F0.wireOp",EDGE,"E21.left");Q59=makeQuery(id+"F0.imprint","IMPRINT",FACE,{"disambiguationData":[TD([[makeQuery(id+"F0.imprint","IMPRINT",EDGE,{"derivedFrom":subQ5}),1.0]])]});}
            var Q60;
            {var subQ0=sQuery(id+"F0.wireOp",EDGE,"E21.top");var subQ1=sQuery(id+"F0.wireOp",EDGE,"E20.left");var subQ2=makeQuery(id+"F0.imprint","INTERSECT",VERTEX,{"derivedFrom":[subQ1,subQ0]});Q60=makeQuery(id+"F0.imprint","IMPRINT",FACE,{"disambiguationData":[TD([[makeQuery(id+"F0.imprint","IMPRINT",EDGE,{"disambiguationData":[TD([[subQ2,-1.0]])],"derivedFrom":subQ1}),1.0]])]});}
            var Q61;
            {var subQ0=sQuery(id+"F0.wireOp",EDGE,"E20.bottom");Q61=makeQuery(id+"F0.imprint","IMPRINT",FACE,{"disambiguationData":[TD([[makeQuery(id+"F0.imprint","IMPRINT",EDGE,{"derivedFrom":subQ0}),-1.0]])]});}
            var Q62;
            {var subQ0=sQuery(id+"F0.wireOp",EDGE,"E52");Q62=makeQuery(id+"F0.imprint","IMPRINT",FACE,{"disambiguationData":[TD([[makeQuery(id+"F0.imprint","IMPRINT",EDGE,{"derivedFrom":subQ0}),-1.0]])]});}
            var Q63;
            {var subQ0=sQuery(id+"F0.wireOp",EDGE,"E53");Q63=makeQuery(id+"F0.imprint","IMPRINT",FACE,{"disambiguationData":[TD([[makeQuery(id+"F0.imprint","IMPRINT",EDGE,{"derivedFrom":subQ0}),-1.0]])]});}
            var Q64;
            {var subQ0=sQuery(id+"F0.wireOp",EDGE,"E56");Q64=makeQuery(id+"F0.imprint","IMPRINT",FACE,{"disambiguationData":[TD([[makeQuery(id+"F0.imprint","IMPRINT",EDGE,{"derivedFrom":subQ0}),-1.0]])]});}
            var Q65;
            {var subQ5=sQuery(id+"F0.wireOp",EDGE,"E24.right");Q65=makeQuery(id+"F0.imprint","IMPRINT",FACE,{"disambiguationData":[TD([[makeQuery(id+"F0.imprint","IMPRINT",EDGE,{"derivedFrom":subQ5}),-1.0]])]});}
            var Q66;
            {var subQ0=sQuery(id+"F0.wireOp",EDGE,"E59");Q66=makeQuery(id+"F0.imprint","IMPRINT",FACE,{"disambiguationData":[TD([[makeQuery(id+"F0.imprint","IMPRINT",EDGE,{"derivedFrom":subQ0}),-1.0]])]});}
            var Q67;
            {var subQ0=sQuery(id+"F0.wireOp",EDGE,"E23.top");Q67=makeQuery(id+"F0.imprint","IMPRINT",FACE,{"disambiguationData":[TD([[makeQuery(id+"F0.imprint","IMPRINT",EDGE,{"derivedFrom":subQ0}),1.0]])]});}
            var Q68;
            {var subQ0=sQuery(id+"F0.wireOp",EDGE,"E24.top");var subQ1=sQuery(id+"F0.wireOp",EDGE,"E23.left");var subQ2=makeQuery(id+"F0.imprint","INTERSECT",VERTEX,{"derivedFrom":[subQ1,subQ0]});Q68=makeQuery(id+"F0.imprint","IMPRINT",FACE,{"disambiguationData":[TD([[makeQuery(id+"F0.imprint","IMPRINT",EDGE,{"disambiguationData":[TD([[subQ2,-1.0]])],"derivedFrom":subQ1}),1.0]])]});}
            var Q69;
            {var subQ0=sQuery(id+"F0.wireOp",EDGE,"E23.bottom");Q69=makeQuery(id+"F0.imprint","IMPRINT",FACE,{"disambiguationData":[TD([[makeQuery(id+"F0.imprint","IMPRINT",EDGE,{"derivedFrom":subQ0}),-1.0]])]});}
            var Q70;
            {var subQ0=sQuery(id+"F0.wireOp",EDGE,"E57");Q70=makeQuery(id+"F0.imprint","IMPRINT",FACE,{"disambiguationData":[TD([[makeQuery(id+"F0.imprint","IMPRINT",EDGE,{"derivedFrom":subQ0}),-1.0]])]});}
            var Q71;
            {var subQ5=sQuery(id+"F0.wireOp",EDGE,"E24.left");Q71=makeQuery(id+"F0.imprint","IMPRINT",FACE,{"disambiguationData":[TD([[makeQuery(id+"F0.imprint","IMPRINT",EDGE,{"derivedFrom":subQ5}),1.0]])]});}
            var Q72;
            {var subQ0=sQuery(id+"F0.wireOp",EDGE,"E58");Q72=makeQuery(id+"F0.imprint","IMPRINT",FACE,{"disambiguationData":[TD([[makeQuery(id+"F0.imprint","IMPRINT",EDGE,{"derivedFrom":subQ0}),-1.0]])]});}
            var Q73;
            {var subQ5=sQuery(id+"F0.wireOp",EDGE,"E27.right");Q73=makeQuery(id+"F0.imprint","IMPRINT",FACE,{"disambiguationData":[TD([[makeQuery(id+"F0.imprint","IMPRINT",EDGE,{"derivedFrom":subQ5}),-1.0]])]});}
            var Q74;
            {var subQ0=sQuery(id+"F0.wireOp",EDGE,"E63");Q74=makeQuery(id+"F0.imprint","IMPRINT",FACE,{"disambiguationData":[TD([[makeQuery(id+"F0.imprint","IMPRINT",EDGE,{"derivedFrom":subQ0}),-1.0]])]});}
            var Q75;
            {var subQ0=sQuery(id+"F0.wireOp",EDGE,"E26.top");Q75=makeQuery(id+"F0.imprint","IMPRINT",FACE,{"disambiguationData":[TD([[makeQuery(id+"F0.imprint","IMPRINT",EDGE,{"derivedFrom":subQ0}),1.0]])]});}
            var Q76;
            {var subQ5=sQuery(id+"F0.wireOp",EDGE,"E27.left");Q76=makeQuery(id+"F0.imprint","IMPRINT",FACE,{"disambiguationData":[TD([[makeQuery(id+"F0.imprint","IMPRINT",EDGE,{"derivedFrom":subQ5}),1.0]])]});}
            var Q77;
            {var subQ0=sQuery(id+"F0.wireOp",EDGE,"E26.bottom");Q77=makeQuery(id+"F0.imprint","IMPRINT",FACE,{"disambiguationData":[TD([[makeQuery(id+"F0.imprint","IMPRINT",EDGE,{"derivedFrom":subQ0}),-1.0]])]});}
            var Q78;
            {var subQ0=sQuery(id+"F0.wireOp",EDGE,"E60");Q78=makeQuery(id+"F0.imprint","IMPRINT",FACE,{"disambiguationData":[TD([[makeQuery(id+"F0.imprint","IMPRINT",EDGE,{"derivedFrom":subQ0}),-1.0]])]});}
            var Q79;
            {var subQ0=sQuery(id+"F0.wireOp",EDGE,"E27.top");var subQ1=sQuery(id+"F0.wireOp",EDGE,"E26.left");var subQ2=makeQuery(id+"F0.imprint","INTERSECT",VERTEX,{"derivedFrom":[subQ1,subQ0]});Q79=makeQuery(id+"F0.imprint","IMPRINT",FACE,{"disambiguationData":[TD([[makeQuery(id+"F0.imprint","IMPRINT",EDGE,{"disambiguationData":[TD([[subQ2,-1.0]])],"derivedFrom":subQ1}),1.0]])]});}
            var Q80;
            {var subQ0=sQuery(id+"F0.wireOp",EDGE,"E61");Q80=makeQuery(id+"F0.imprint","IMPRINT",FACE,{"disambiguationData":[TD([[makeQuery(id+"F0.imprint","IMPRINT",EDGE,{"derivedFrom":subQ0}),-1.0]])]});}
            var Q81;
            {var subQ0=sQuery(id+"F0.wireOp",EDGE,"E62");Q81=makeQuery(id+"F0.imprint","IMPRINT",FACE,{"disambiguationData":[TD([[makeQuery(id+"F0.imprint","IMPRINT",EDGE,{"derivedFrom":subQ0}),-1.0]])]});}
            extrude(context, id + "F2", {"entities" : qUnion([Q0, Q1, Q2, Q3, Q4, Q5, Q6, Q7, Q8, Q9, Q10, Q11, Q12, Q13, Q14, Q15, Q16, Q17, Q18, Q19, Q20, Q21, Q22, Q23, Q24, Q25, Q26, Q27, Q28, Q29, Q30, Q31, Q32, Q33, Q34, Q35, Q36, Q37, Q38, Q39, Q40, Q41, Q42, Q43, Q44, Q45, Q46, Q47, Q48, Q49, Q50, Q51, Q52, Q53, Q54, Q55, Q56, Q57, Q58, Q59, Q60, Q61, Q62, Q63, Q64, Q65, Q66, Q67, Q68, Q69, Q70, Q71, Q72, Q73, Q74, Q75, Q76, Q77, Q78, Q79, Q80, Q81]), "depth" : 1 * mm});
        }
        {
            var Q0;
            Q0=makeQuery(id+"F1.opExtrude","SWEPT_EDGE",EDGE,{"disambiguationData":[OSD([sQuery(id+"F0.wireOp",EDGE,"E0.top"),sQuery(id+"F0.wireOp",EDGE,"E0.right")])]});
            var Q1;
            Q1=makeQuery(id+"F1.opExtrude","SWEPT_EDGE",EDGE,{"disambiguationData":[OSD([sQuery(id+"F0.wireOp",EDGE,"E0.bottom"),sQuery(id+"F0.wireOp",EDGE,"E0.left")])]});
            var Q2;
            Q2=makeQuery(id+"F1.opExtrude","SWEPT_EDGE",EDGE,{"disambiguationData":[OSD([sQuery(id+"F0.wireOp",EDGE,"E0.top"),sQuery(id+"F0.wireOp",EDGE,"E0.left")])]});
            var Q3;
            Q3=makeQuery(id+"F2.opExtrude","SWEPT_EDGE",EDGE,{"disambiguationData":[OSD([sQuery(id+"F0.wireOp",EDGE,"E0.top"),sQuery(id+"F0.wireOp",EDGE,"E0.left")])]});
            var Q4;
            Q4=makeQuery(id+"F2.opExtrude","SWEPT_EDGE",EDGE,{"disambiguationData":[OSD([sQuery(id+"F0.wireOp",EDGE,"E0.bottom"),sQuery(id+"F0.wireOp",EDGE,"E0.left")])]});
            var Q5;
            Q5=makeQuery(id+"F1.opExtrude","SWEPT_EDGE",EDGE,{"disambiguationData":[OSD([sQuery(id+"F0.wireOp",EDGE,"E0.bottom"),sQuery(id+"F0.wireOp",EDGE,"E0.right")])]});
            var Q6;
            Q6=makeQuery(id+"F2.opExtrude","SWEPT_EDGE",EDGE,{"disambiguationData":[OSD([sQuery(id+"F0.wireOp",EDGE,"E0.bottom"),sQuery(id+"F0.wireOp",EDGE,"E0.right")])]});
            var Q7;
            Q7=makeQuery(id+"F2.opExtrude","SWEPT_EDGE",EDGE,{"disambiguationData":[OSD([sQuery(id+"F0.wireOp",EDGE,"E0.top"),sQuery(id+"F0.wireOp",EDGE,"E0.right")])]});
            fillet(context, id + "F3", {"entities" : qUnion([Q0, Q1, Q2, Q3, Q4, Q5, Q6, Q7]), "radius" : 5 * mm, "tangentPropagation" : true, "allowEdgeOverflow" : false});
        }
        {
            var Q0;
            Q0=makeQuery(id+"F1.opExtrude","CAP_EDGE",EDGE,{"disambiguationData":[OSD([sQuery(id+"F0.wireOp",EDGE,"E0.bottom")])],"isStart":false});
            var Q1;
            Q1=makeQuery(id+"F1.opExtrude","CAP_EDGE",EDGE,{"disambiguationData":[OSD([sQuery(id+"F0.wireOp",EDGE,"E0.top")])],"isStart":false});
            chamfer(context, id + "F4", {"entities" : qUnion([Q0, Q1]), "width" : 5 * mm, "tangentPropagation" : true});
        }
        {
            var Q0;
            Q0=makeQuery(id+"F2.opExtrude","SWEPT_BODY",BODY,{"disambiguationData":[OSD([sQuery(id+"F0.wireOp",EDGE,"E0.bottom"),sQuery(id+"F0.wireOp",EDGE,"E0.top"),sQuery(id+"F0.wireOp",EDGE,"E0.left"),sQuery(id+"F0.wireOp",EDGE,"E0.right")])]});
            transform(context, id + "F5", {"entities" : qUnion([Q0]), "transformType" : TransformType.TRANSLATION_3D, "dx" : 0 * mm, "dy" : -11.5 * mm, "dz" : 0 * mm, "makeCopy" : true});
        }
        {
            var Q0;
            Q0=makeQuery(id+"F5.opPattern","COPY",BODY,{"derivedFrom":makeQuery(id+"F2.opExtrude","SWEPT_BODY",BODY,{"disambiguationData":[OSD([sQuery(id+"F0.wireOp",EDGE,"E0.bottom"),sQuery(id+"F0.wireOp",EDGE,"E0.top"),sQuery(id+"F0.wireOp",EDGE,"E0.left"),sQuery(id+"F0.wireOp",EDGE,"E0.right")])]}),"instanceName":"1"});
            transform(context, id + "F6", {"entities" : qUnion([Q0]), "transformType" : TransformType.TRANSLATION_3D, "dx" : 0 * mm, "dy" : -11.5 * mm, "dz" : 0 * mm, "makeCopy" : true});
        }
        {
            var Q0;
            Q0=makeQuery(id+"F6.opPattern","COPY",BODY,{"derivedFrom":makeQuery(id+"F5.opPattern","COPY",BODY,{"derivedFrom":makeQuery(id+"F2.opExtrude","SWEPT_BODY",BODY,{"disambiguationData":[OSD([sQuery(id+"F0.wireOp",EDGE,"E0.bottom"),sQuery(id+"F0.wireOp",EDGE,"E0.top"),sQuery(id+"F0.wireOp",EDGE,"E0.left"),sQuery(id+"F0.wireOp",EDGE,"E0.right")])]}),"instanceName":"1"}),"instanceName":"1"});
            transform(context, id + "F7", {"entities" : qUnion([Q0]), "transformType" : TransformType.TRANSLATION_3D, "dx" : 0 * mm, "dy" : -11.5 * mm, "dz" : 0 * mm, "makeCopy" : true});
        }
        {
            var Q0;
            Q0=makeQuery(id+"F7.opPattern","COPY",BODY,{"derivedFrom":makeQuery(id+"F6.opPattern","COPY",BODY,{"derivedFrom":makeQuery(id+"F5.opPattern","COPY",BODY,{"derivedFrom":makeQuery(id+"F2.opExtrude","SWEPT_BODY",BODY,{"disambiguationData":[OSD([sQuery(id+"F0.wireOp",EDGE,"E0.bottom"),sQuery(id+"F0.wireOp",EDGE,"E0.top"),sQuery(id+"F0.wireOp",EDGE,"E0.left"),sQuery(id+"F0.wireOp",EDGE,"E0.right")])]}),"instanceName":"1"}),"instanceName":"1"}),"instanceName":"1"});
            transform(context, id + "F8", {"entities" : qUnion([Q0]), "transformType" : TransformType.TRANSLATION_3D, "dx" : 0 * mm, "dy" : -11.5 * mm, "dz" : 0 * mm, "makeCopy" : true});
        }
    });
